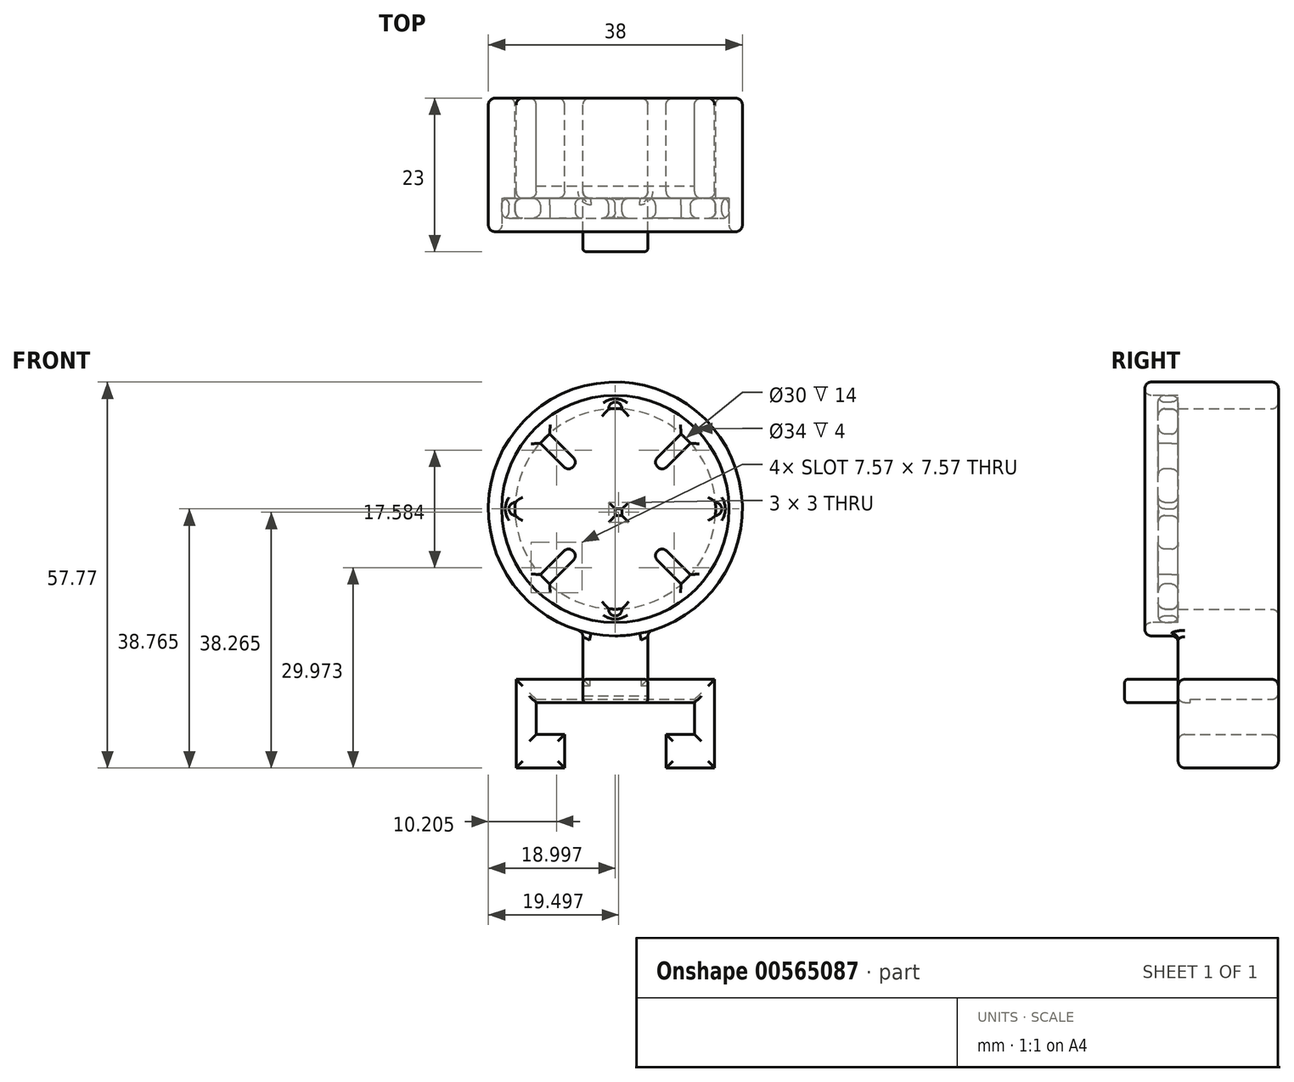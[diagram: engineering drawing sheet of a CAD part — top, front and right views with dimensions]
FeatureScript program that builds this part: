
annotation { "Feature Type Name" : "Feature", "Feature Type Description" : "" }
export const myFeature = defineFeature(function(context is Context, id is Id, definition is map)
    precondition{}
    {
        {
            var Q0;
            Q0=qCreatedBy(makeId("Front.planeOp"),FACE);
            var sketch = newSketch(context, id + "F0", { "sketchPlane" : qUnion([Q0])});
            skLineSegment(sketch, "E0", {"start": v(-3.95, 1.2) * mm, "end": v(-3.95, 6.2) * mm});
            skLineSegment(sketch, "E1", {"start": v(-3.95, 6.2) * mm, "end": v(-8.2, 6.2) * mm});
            skLineSegment(sketch, "E2", {"start": v(-8.2, 6.2) * mm, "end": v(-8.2, 11.46) * mm});
            skLineSegment(sketch, "E3", {"start": v(-8.2, 11.46) * mm, "end": v(15.5, 11.46) * mm});
            skLineSegment(sketch, "E4", {"start": v(15.5, 11.46) * mm, "end": v(15.5, 6.2) * mm});
            skLineSegment(sketch, "E5", {"start": v(15.5, 6.2) * mm, "end": v(11.25, 6.2) * mm});
            skLineSegment(sketch, "E6", {"start": v(11.25, 6.2) * mm, "end": v(11.25, 1.2) * mm});
            skLineSegment(sketch, "E7", {"start": v(18.5, 1.2) * mm, "end": v(18.5, 14.46) * mm});
            skLineSegment(sketch, "E8", {"start": v(18.5, 14.46) * mm, "end": v(-11.2, 14.46) * mm});
            skLineSegment(sketch, "E9", {"start": v(-11.2, 14.46) * mm, "end": v(-11.2, 1.2) * mm});
            skLineSegment(sketch, "E10", {"start": v(-11.2, 1.2) * mm, "end": v(-3.95, 1.2) * mm});
            skLineSegment(sketch, "E11", {"start": v(3.65, 14.46) * mm, "end": v(3.65, -1.28) * mm, "construction": true});
            skLineSegment(sketch, "E12", {"start": v(11.25, 1.2) * mm, "end": v(18.5, 1.2) * mm});
            skSolve(sketch);
        }
        {
            var Q0;
            Q0 = qSketchRegion(id + "F0", true);
            extrude(context, id + "F1", {"entities" : qUnion([Q0]), "depth" : 15 * mm, "offsetDistance" : 25 * mm});
        }
        {
            var Q0;
            Q0=makeQuery(id+"F1.opExtrude","SWEPT_FACE",FACE,{"disambiguationData":[OSD([sQuery(id+"F0.wireOp",EDGE,"E8")])]});
            var sketch = newSketch(context, id + "F2", { "sketchPlane" : qUnion([Q0])});
            skLineSegment(sketch, "E13.bottom", {"start": v(-1.2, -15) * mm, "end": v(8.5, -15) * mm});
            skLineSegment(sketch, "E13.top", {"start": v(-1.2, 0) * mm, "end": v(8.5, 0) * mm});
            skLineSegment(sketch, "E13.left", {"start": v(-1.2, -15) * mm, "end": v(-1.2, 0) * mm});
            skLineSegment(sketch, "E13.right", {"start": v(8.5, -15) * mm, "end": v(8.5, 0) * mm});
            skSolve(sketch);
        }
        {
            var Q0;
            Q0=makeQuery(id+"F2.imprint","IMPRINT",FACE,{"disambiguationData":[TD([[makeQuery(id+"F2.imprint","IMPRINT",EDGE,{"derivedFrom":sQuery(id+"F2.wireOp",EDGE,"E13.bottom")}),-1.0]])]});
            extrude(context, id + "F3", {"entities" : qUnion([Q0]), "operationType" : NewBodyOperationType.ADD, "depth" : 8 * mm, "offsetDistance" : 25 * mm});
        }
        {
            var Q0;
            Q0=makeQuery(id+"F3.boolean.opBoolean","MERGE",FACE,{"derivedFrom":[makeQuery(id+"F1.opExtrude","CAP_FACE",FACE,{"disambiguationData":[OSD([sQuery(id+"F0.wireOp",EDGE,"E0"),sQuery(id+"F0.wireOp",EDGE,"E1"),sQuery(id+"F0.wireOp",EDGE,"E2"),sQuery(id+"F0.wireOp",EDGE,"E3"),sQuery(id+"F0.wireOp",EDGE,"E4"),sQuery(id+"F0.wireOp",EDGE,"E5"),sQuery(id+"F0.wireOp",EDGE,"E6"),sQuery(id+"F0.wireOp",EDGE,"E7"),sQuery(id+"F0.wireOp",EDGE,"E8"),sQuery(id+"F0.wireOp",EDGE,"E9"),sQuery(id+"F0.wireOp",EDGE,"E10"),sQuery(id+"F0.wireOp",EDGE,"E12")])],"isStart":false}),makeQuery(id+"F3.opExtrude","SWEPT_FACE",FACE,{"disambiguationData":[OSD([sQuery(id+"F2.wireOp",EDGE,"E13.bottom")])]})]});
            var sketch = newSketch(context, id + "F4", { "sketchPlane" : qUnion([Q0])});
            skCircle(sketch, "E14", {"center": v(3.65, 39.97) * mm, "radius": 19 * mm});
            skPoint(sketch, "E14.centerSnap0", {"position": v(3.65, 22.46) * mm});
            skCircle(sketch, "E15", {"center": v(3.65, 39.97) * mm, "radius": 15 * mm});
            skSolve(sketch);
        }
        {
            var Q0;
            Q0 = qSketchRegion(id + "F4", true);
            extrude(context, id + "F5", {"entities" : qUnion([Q0]), "operationType" : NewBodyOperationType.ADD, "depth" : 5 * mm, "offsetDistance" : 25 * mm});
        }
        {
            var Q0;
            Q0=makeQuery(id+"F5.opExtrude","CAP_FACE",FACE,{"disambiguationData":[OSD([sQuery(id+"F4.wireOp",EDGE,"E14"),sQuery(id+"F4.wireOp",EDGE,"E15")])],"isStart":true});
            extrude(context, id + "F6", {"entities" : qUnion([Q0]), "operationType" : NewBodyOperationType.ADD, "depth" : 15 * mm, "offsetDistance" : 25 * mm});
        }
        {
            var Q0;
            Q0=makeQuery(id+"F5.opExtrude","CAP_FACE",FACE,{"disambiguationData":[OSD([sQuery(id+"F4.wireOp",EDGE,"E14"),sQuery(id+"F4.wireOp",EDGE,"E15")])],"isStart":false});
            var sketch = newSketch(context, id + "F7", { "sketchPlane" : qUnion([Q0])});
            skCircle(sketch, "E16", {"center": v(3.65, 39.97) * mm, "radius": 17 * mm});
            skSolve(sketch);
        }
        {
            var Q0;
            Q0 = qSketchRegion(id + "F7", true);
            extrude(context, id + "F8", {"entities" : qUnion([Q0]), "operationType" : NewBodyOperationType.REMOVE, "oppositeDirection" : true, "depth" : 5 * mm, "offsetDistance" : 25 * mm});
        }
        {
            var Q0;
            Q0=makeQuery(id+"F1.opExtrude","SWEPT_FACE",FACE,{"disambiguationData":[OSD([sQuery(id+"F0.wireOp",EDGE,"E3")])]});
            var sketch = newSketch(context, id + "F9", { "sketchPlane" : qUnion([Q0])});
            skLineSegment(sketch, "E17.bottom", {"start": v(-8.2, 15) * mm, "end": v(15.5, 15) * mm});
            skLineSegment(sketch, "E17.top", {"start": v(-8.2, 13.16) * mm, "end": v(15.5, 13.16) * mm});
            skLineSegment(sketch, "E17.left", {"start": v(-8.2, 15) * mm, "end": v(-8.2, 13.16) * mm});
            skLineSegment(sketch, "E17.right", {"start": v(15.5, 15) * mm, "end": v(15.5, 13.16) * mm});
            skSolve(sketch);
        }
        {
            var Q0;
            Q0 = qSketchRegion(id + "F9", true);
            extrude(context, id + "F10", {"entities" : qUnion([Q0]), "operationType" : NewBodyOperationType.ADD, "depth" : 0.5 * mm, "offsetDistance" : 25 * mm});
        }
        {
            var Q0;
            Q0=makeQuery(id+"F10.boolean.opBoolean","MERGE",FACE,{"derivedFrom":[makeQuery(id+"F3.boolean.opBoolean","MERGE",FACE,{"derivedFrom":[makeQuery(id+"F1.opExtrude","CAP_FACE",FACE,{"disambiguationData":[OSD([sQuery(id+"F0.wireOp",EDGE,"E0"),sQuery(id+"F0.wireOp",EDGE,"E1"),sQuery(id+"F0.wireOp",EDGE,"E2"),sQuery(id+"F0.wireOp",EDGE,"E3"),sQuery(id+"F0.wireOp",EDGE,"E4"),sQuery(id+"F0.wireOp",EDGE,"E5"),sQuery(id+"F0.wireOp",EDGE,"E6"),sQuery(id+"F0.wireOp",EDGE,"E7"),sQuery(id+"F0.wireOp",EDGE,"E8"),sQuery(id+"F0.wireOp",EDGE,"E9"),sQuery(id+"F0.wireOp",EDGE,"E10"),sQuery(id+"F0.wireOp",EDGE,"E12")])],"isStart":false}),makeQuery(id+"F3.opExtrude","SWEPT_FACE",FACE,{"disambiguationData":[OSD([sQuery(id+"F2.wireOp",EDGE,"E13.bottom")])]})]}),makeQuery(id+"F10.opExtrude","SWEPT_FACE",FACE,{"disambiguationData":[OSD([sQuery(id+"F9.wireOp",EDGE,"E17.bottom")])]})]});
            var sketch = newSketch(context, id + "F11", { "sketchPlane" : qUnion([Q0])});
            skLineSegment(sketch, "E18.bottom", {"start": v(-1.2, 14.46) * mm, "end": v(8.5, 14.46) * mm});
            skLineSegment(sketch, "E18.top", {"start": v(-1.2, 10.96) * mm, "end": v(8.5, 10.96) * mm});
            skLineSegment(sketch, "E18.left", {"start": v(-1.2, 14.46) * mm, "end": v(-1.2, 10.96) * mm});
            skLineSegment(sketch, "E18.right", {"start": v(8.5, 14.46) * mm, "end": v(8.5, 10.96) * mm});
            skSolve(sketch);
        }
        {
            var Q0;
            Q0=makeQuery(id+"F3.boolean.opBoolean","MERGE",FACE,{"derivedFrom":[makeQuery(id+"F1.opExtrude","CAP_FACE",FACE,{"disambiguationData":[OSD([sQuery(id+"F0.wireOp",EDGE,"E0"),sQuery(id+"F0.wireOp",EDGE,"E1"),sQuery(id+"F0.wireOp",EDGE,"E2"),sQuery(id+"F0.wireOp",EDGE,"E3"),sQuery(id+"F0.wireOp",EDGE,"E4"),sQuery(id+"F0.wireOp",EDGE,"E5"),sQuery(id+"F0.wireOp",EDGE,"E6"),sQuery(id+"F0.wireOp",EDGE,"E7"),sQuery(id+"F0.wireOp",EDGE,"E8"),sQuery(id+"F0.wireOp",EDGE,"E9"),sQuery(id+"F0.wireOp",EDGE,"E10"),sQuery(id+"F0.wireOp",EDGE,"E12")])],"isStart":false}),makeQuery(id+"F3.opExtrude","SWEPT_FACE",FACE,{"disambiguationData":[OSD([sQuery(id+"F2.wireOp",EDGE,"E13.bottom")])]})]});
            var Q1;
            Q1=makeQuery(id+"F5.opExtrude","CAP_FACE",FACE,{"disambiguationData":[OSD([sQuery(id+"F4.wireOp",EDGE,"E14"),sQuery(id+"F4.wireOp",EDGE,"E15")])],"isStart":false});
            var Q2;
            {var subQ0=sQuery(id+"F4.wireOp",EDGE,"E14");Q2=makeQuery(id+"F6.boolean.opBoolean","MERGE",FACE,{"derivedFrom":[makeQuery(id+"F5.opExtrude","SWEPT_FACE",FACE,{"disambiguationData":[OSD([subQ0])]}),makeQuery(id+"F6.opExtrude","SWEPT_FACE",FACE,{"disambiguationData":[OSD([subQ0])]})]});}
            var Q3;
            Q3=makeQuery(id+"F6.boolean.opBoolean","MERGE",FACE,{"derivedFrom":[makeQuery(id+"F3.boolean.opBoolean","MERGE",FACE,{"derivedFrom":[makeQuery(id+"F1.opExtrude","CAP_FACE",FACE,{"disambiguationData":[OSD([sQuery(id+"F0.wireOp",EDGE,"E0"),sQuery(id+"F0.wireOp",EDGE,"E1"),sQuery(id+"F0.wireOp",EDGE,"E2"),sQuery(id+"F0.wireOp",EDGE,"E3"),sQuery(id+"F0.wireOp",EDGE,"E4"),sQuery(id+"F0.wireOp",EDGE,"E5"),sQuery(id+"F0.wireOp",EDGE,"E6"),sQuery(id+"F0.wireOp",EDGE,"E7"),sQuery(id+"F0.wireOp",EDGE,"E8"),sQuery(id+"F0.wireOp",EDGE,"E9"),sQuery(id+"F0.wireOp",EDGE,"E10"),sQuery(id+"F0.wireOp",EDGE,"E12")])],"isStart":true}),makeQuery(id+"F3.opExtrude","SWEPT_FACE",FACE,{"disambiguationData":[OSD([sQuery(id+"F2.wireOp",EDGE,"E13.top")])]})]}),makeQuery(id+"F6.opExtrude","CAP_FACE",FACE,{"disambiguationData":[OSD([sQuery(id+"F4.wireOp",EDGE,"E14"),sQuery(id+"F4.wireOp",EDGE,"E15")])],"isStart":false})]});
            fillet(context, id + "F12", {"entities" : qUnion([Q0, Q1, Q2, Q3]), "radius" : 1 * mm, "tangentPropagation" : true, "allowEdgeOverflow" : false});
        }
        {
            var Q0;
            Q0 = qSketchRegion(id + "F11", true);
            extrude(context, id + "F13", {"entities" : qUnion([Q0]), "operationType" : NewBodyOperationType.ADD, "depth" : 8 * mm, "offsetDistance" : 25 * mm});
        }
        {
            var Q0;
            Q0=makeQuery(id+"F13.opExtrude","SWEPT_FACE",FACE,{"disambiguationData":[OSD([sQuery(id+"F11.wireOp",EDGE,"E18.top")])]});
            var Q1;
            Q1=makeQuery(id+"F13.opExtrude","CAP_FACE",FACE,{"disambiguationData":[OSD([sQuery(id+"F11.wireOp",EDGE,"E18.bottom"),sQuery(id+"F11.wireOp",EDGE,"E18.top"),sQuery(id+"F11.wireOp",EDGE,"E18.left"),sQuery(id+"F11.wireOp",EDGE,"E18.right")])],"isStart":false});
            var Q2;
            Q2=makeQuery(id+"F13.opExtrude","SWEPT_EDGE",EDGE,{"disambiguationData":[OSD([sQuery(id+"F0.wireOp",EDGE,"E8"),sQuery(id+"F2.wireOp",EDGE,"E13.bottom"),sQuery(id+"F2.wireOp",EDGE,"E13.right"),sQuery(id+"F11.wireOp",EDGE,"E18.bottom"),sQuery(id+"F11.wireOp",EDGE,"E18.right")])]});
            var Q3;
            Q3=makeQuery(id+"F13.opExtrude","SWEPT_EDGE",EDGE,{"disambiguationData":[OSD([sQuery(id+"F0.wireOp",EDGE,"E8"),sQuery(id+"F2.wireOp",EDGE,"E13.bottom"),sQuery(id+"F2.wireOp",EDGE,"E13.left"),sQuery(id+"F11.wireOp",EDGE,"E18.bottom"),sQuery(id+"F11.wireOp",EDGE,"E18.left")])]});
            fillet(context, id + "F14", {"entities" : qUnion([Q0, Q1, Q2, Q3]), "radius" : 0.5 * mm, "tangentPropagation" : true, "allowEdgeOverflow" : false});
        }
        {
            var Q0;
            Q0=makeQuery(id+"F8.boolean.opBoolean","COPY",FACE,{"derivedFrom":makeQuery(id+"F8.opExtrude","CAP_FACE",FACE,{"disambiguationData":[OSD([sQuery(id+"F7.wireOp",EDGE,"E16")])],"isStart":false})});
            var sketch = newSketch(context, id + "F15", { "sketchPlane" : qUnion([Q0])});
            skCircle(sketch, "E19", {"center": v(3.65, 39.97) * mm, "radius": 16.93 * mm});
            skCircle(sketch, "E20", {"center": v(3.65, 39.97) * mm, "radius": 14.91 * mm});
            skCircle(sketch, "E21", {"center": v(3.65, 39.97) * mm, "radius": 1.82 * mm});
            skLineSegment(sketch, "E22", {"start": v(3.65, 39.97) * mm, "end": v(3.65, 54.97) * mm});
            skArc(sketch, "E23.0.startCap", {"start": v(4.65, 39.97) * mm, "mid": v(3.65, 38.97) * mm, "end": v(2.65, 39.97) * mm});
            skArc(sketch, "E23.0.endCap", {"start": v(2.65, 54.97) * mm, "mid": v(3.65, 55.97) * mm, "end": v(4.65, 54.97) * mm});
            skLineSegment(sketch, "E23.0.left", {"start": v(2.65, 39.97) * mm, "end": v(2.65, 54.97) * mm});
            skLineSegment(sketch, "E23.0.right", {"start": v(4.65, 39.97) * mm, "end": v(4.65, 54.97) * mm});
            skLineSegment(sketch, "E24", {"start": v(3.65, 39.97) * mm, "end": v(18.56, 39.97) * mm});
            skLineSegment(sketch, "E25", {"start": v(3.65, 39.97) * mm, "end": v(-11.26, 39.97) * mm});
            skLineSegment(sketch, "E26", {"start": v(3.65, 39.97) * mm, "end": v(3.65, 24.97) * mm});
            skArc(sketch, "E27.0.startCap", {"start": v(3.65, 40.97) * mm, "mid": v(4.65, 39.97) * mm, "end": v(3.65, 38.97) * mm});
            skArc(sketch, "E27.0.endCap", {"start": v(-11.26, 38.97) * mm, "mid": v(-12.26, 39.97) * mm, "end": v(-11.26, 40.97) * mm});
            skLineSegment(sketch, "E27.0.left", {"start": v(3.65, 38.97) * mm, "end": v(-11.26, 38.97) * mm});
            skLineSegment(sketch, "E27.0.right", {"start": v(3.65, 40.97) * mm, "end": v(-11.26, 40.97) * mm});
            skArc(sketch, "E27.1.startCap", {"start": v(2.65, 39.97) * mm, "mid": v(3.65, 40.97) * mm, "end": v(4.65, 39.97) * mm});
            skArc(sketch, "E27.1.endCap", {"start": v(4.65, 24.97) * mm, "mid": v(3.65, 23.97) * mm, "end": v(2.65, 24.97) * mm});
            skLineSegment(sketch, "E27.1.left", {"start": v(4.65, 39.97) * mm, "end": v(4.65, 24.97) * mm});
            skLineSegment(sketch, "E27.1.right", {"start": v(2.65, 39.97) * mm, "end": v(2.65, 24.97) * mm});
            skArc(sketch, "E27.2.startCap", {"start": v(3.65, 38.97) * mm, "mid": v(2.65, 39.97) * mm, "end": v(3.65, 40.97) * mm});
            skArc(sketch, "E27.2.endCap", {"start": v(18.56, 40.97) * mm, "mid": v(19.56, 39.97) * mm, "end": v(18.56, 38.97) * mm});
            skLineSegment(sketch, "E27.2.left", {"start": v(3.65, 40.97) * mm, "end": v(18.56, 40.97) * mm});
            skLineSegment(sketch, "E27.2.right", {"start": v(3.65, 38.97) * mm, "end": v(18.56, 38.97) * mm});
            skSolve(sketch);
        }
        {
            var Q0;
            {var subQ0=sQuery(id+"F15.wireOp",EDGE,"E27.2.left");var subQ7=sQuery(id+"F15.wireOp",EDGE,"E20");var subQ10=makeQuery(id+"F15.imprint","INTERSECT",VERTEX,{"derivedFrom":[subQ7,subQ0]});Q0=makeQuery(id+"F15.imprint","IMPRINT",FACE,{"disambiguationData":[TD([[makeQuery(id+"F15.imprint","IMPRINT",EDGE,{"disambiguationData":[TD([[subQ10,-1.0]])],"derivedFrom":subQ7}),-1.0]])]});}
            var Q1;
            {var subQ3=sQuery(id+"F15.wireOp",EDGE,"E20");var subQ8=sQuery(id+"F15.wireOp",EDGE,"E23.0.left");var subQ9=makeQuery(id+"F15.imprint","INTERSECT",VERTEX,{"derivedFrom":[subQ3,subQ8]});Q1=makeQuery(id+"F15.imprint","IMPRINT",FACE,{"disambiguationData":[TD([[makeQuery(id+"F15.imprint","IMPRINT",EDGE,{"disambiguationData":[TD([[subQ9,-1.0]])],"derivedFrom":subQ3}),-1.0]])]});}
            var Q2;
            {var subQ1=sQuery(id+"F15.wireOp",EDGE,"E20");var subQ6=sQuery(id+"F15.wireOp",EDGE,"E27.0.left");var subQ9=makeQuery(id+"F15.imprint","INTERSECT",VERTEX,{"derivedFrom":[subQ1,subQ6]});Q2=makeQuery(id+"F15.imprint","IMPRINT",FACE,{"disambiguationData":[TD([[makeQuery(id+"F15.imprint","IMPRINT",EDGE,{"disambiguationData":[TD([[subQ9,-1.0]])],"derivedFrom":subQ1}),-1.0]])]});}
            var Q3;
            {var subQ6=sQuery(id+"F15.wireOp",EDGE,"E27.1.left");var subQ7=sQuery(id+"F15.wireOp",EDGE,"E20");var subQ8=makeQuery(id+"F15.imprint","INTERSECT",VERTEX,{"derivedFrom":[subQ7,subQ6]});Q3=makeQuery(id+"F15.imprint","IMPRINT",FACE,{"disambiguationData":[TD([[makeQuery(id+"F15.imprint","IMPRINT",EDGE,{"disambiguationData":[TD([[subQ8,-1.0]])],"derivedFrom":subQ7}),-1.0]])]});}
            var Q4;
            Q4=makeQuery(id+"F15.imprint","IMPRINT",FACE,{"disambiguationData":[TD([[makeQuery(id+"F15.imprint","IMPRINT",EDGE,{"derivedFrom":sQuery(id+"F15.wireOp",EDGE,"E19")}),1.0]])]});
            var Q5;
            {var subQ0=sQuery(id+"F15.wireOp",EDGE,"E24");var subQ1=sQuery(id+"F15.wireOp",EDGE,"E20");var subQ2=makeQuery(id+"F15.imprint","INTERSECT",VERTEX,{"derivedFrom":[subQ1,subQ0]});Q5=makeQuery(id+"F15.imprint","IMPRINT",FACE,{"disambiguationData":[TD([[makeQuery(id+"F15.imprint","IMPRINT",EDGE,{"disambiguationData":[TD([[subQ2,-1.0]])],"derivedFrom":subQ1}),1.0]])]});}
            var Q6;
            {var subQ0=sQuery(id+"F15.wireOp",EDGE,"E24");var subQ1=sQuery(id+"F15.wireOp",EDGE,"E20");var subQ2=makeQuery(id+"F15.imprint","INTERSECT",VERTEX,{"derivedFrom":[subQ1,subQ0]});Q6=makeQuery(id+"F15.imprint","IMPRINT",FACE,{"disambiguationData":[TD([[makeQuery(id+"F15.imprint","IMPRINT",EDGE,{"disambiguationData":[TD([[subQ2,1.0]])],"derivedFrom":subQ1}),1.0]])]});}
            var Q7;
            {var subQ0=sQuery(id+"F15.wireOp",EDGE,"E27.0.right");var subQ1=sQuery(id+"F15.wireOp",EDGE,"E21");var subQ2=makeQuery(id+"F15.imprint","INTERSECT",VERTEX,{"derivedFrom":[subQ1,subQ0]});Q7=makeQuery(id+"F15.imprint","IMPRINT",FACE,{"disambiguationData":[TD([[makeQuery(id+"F15.imprint","IMPRINT",EDGE,{"disambiguationData":[TD([[subQ2,-1.0]])],"derivedFrom":subQ1}),1.0]])]});}
            var Q8;
            Q8=makeQuery(id+"F15.imprint","IMPRINT",FACE,{"disambiguationData":[TD([[makeQuery(id+"F15.imprint","IMPRINT",EDGE,{"derivedFrom":sQuery(id+"F15.wireOp",EDGE,"E19")}),-1.0]])]});
            var Q9;
            {var subQ0=sQuery(id+"F15.wireOp",EDGE,"E26");var subQ1=sQuery(id+"F15.wireOp",EDGE,"E20");var subQ2=makeQuery(id+"F15.imprint","INTERSECT",VERTEX,{"derivedFrom":[subQ1,subQ0]});Q9=makeQuery(id+"F15.imprint","IMPRINT",FACE,{"disambiguationData":[TD([[makeQuery(id+"F15.imprint","IMPRINT",EDGE,{"disambiguationData":[TD([[subQ2,-1.0]])],"derivedFrom":subQ1}),1.0]])]});}
            var Q10;
            {var subQ0=sQuery(id+"F15.wireOp",EDGE,"E27.0.endCap");var subQ1=sQuery(id+"F4.wireOp",EDGE,"E15");var subQ2=makeQuery(id+"F8.boolean.opBoolean","INTERSECT",EDGE,{"derivedFrom":[makeQuery(id+"F6.boolean.opBoolean","MERGE",FACE,{"derivedFrom":[makeQuery(id+"F5.opExtrude","SWEPT_FACE",FACE,{"disambiguationData":[OSD([subQ1])]}),makeQuery(id+"F6.opExtrude","SWEPT_FACE",FACE,{"disambiguationData":[OSD([subQ1])]})]}),makeQuery(id+"F8.opExtrude","CAP_FACE",FACE,{"disambiguationData":[OSD([sQuery(id+"F7.wireOp",EDGE,"E16")])],"isStart":false})]});var subQ3=makeQuery(id+"F15.imprint","INTERSECT",VERTEX,{"disambiguationData":[OD(0.0)],"derivedFrom":[subQ2,subQ0]});Q10=makeQuery(id+"F15.imprint","IMPRINT",FACE,{"disambiguationData":[TD([[makeQuery(id+"F15.imprint","IMPRINT",EDGE,{"disambiguationData":[TD([[subQ3,-1.0]])],"derivedFrom":subQ0}),-1.0]])]});}
            var Q11;
            {var subQ0=sQuery(id+"F15.wireOp",EDGE,"E23.0.right");var subQ1=sQuery(id+"F15.wireOp",EDGE,"E21");var subQ2=makeQuery(id+"F15.imprint","INTERSECT",VERTEX,{"derivedFrom":[subQ1,subQ0]});Q11=makeQuery(id+"F15.imprint","IMPRINT",FACE,{"disambiguationData":[TD([[makeQuery(id+"F15.imprint","IMPRINT",EDGE,{"disambiguationData":[TD([[subQ2,-1.0]])],"derivedFrom":subQ1}),1.0]])]});}
            var Q12;
            {var subQ0=sQuery(id+"F15.wireOp",EDGE,"E23.0.right");var subQ1=sQuery(id+"F15.wireOp",EDGE,"E20");var subQ2=makeQuery(id+"F15.imprint","INTERSECT",VERTEX,{"derivedFrom":[subQ1,subQ0]});Q12=makeQuery(id+"F15.imprint","IMPRINT",FACE,{"disambiguationData":[TD([[makeQuery(id+"F15.imprint","IMPRINT",EDGE,{"disambiguationData":[TD([[subQ2,-1.0]])],"derivedFrom":subQ1}),1.0]])]});}
            var Q13;
            {var subQ0=sQuery(id+"F15.wireOp",EDGE,"E22");var subQ1=sQuery(id+"F15.wireOp",EDGE,"E20");var subQ2=makeQuery(id+"F15.imprint","INTERSECT",VERTEX,{"derivedFrom":[subQ1,subQ0]});Q13=makeQuery(id+"F15.imprint","IMPRINT",FACE,{"disambiguationData":[TD([[makeQuery(id+"F15.imprint","IMPRINT",EDGE,{"disambiguationData":[TD([[subQ2,-1.0]])],"derivedFrom":subQ1}),1.0]])]});}
            var Q14;
            {var subQ0=sQuery(id+"F15.wireOp",EDGE,"E27.1.right");var subQ1=sQuery(id+"F15.wireOp",EDGE,"E20");var subQ2=makeQuery(id+"F15.imprint","INTERSECT",VERTEX,{"derivedFrom":[subQ1,subQ0]});Q14=makeQuery(id+"F15.imprint","IMPRINT",FACE,{"disambiguationData":[TD([[makeQuery(id+"F15.imprint","IMPRINT",EDGE,{"disambiguationData":[TD([[subQ2,-1.0]])],"derivedFrom":subQ1}),1.0]])]});}
            var Q15;
            {var subQ0=sQuery(id+"F15.wireOp",EDGE,"E27.1.right");var subQ1=sQuery(id+"F15.wireOp",EDGE,"E21");var subQ2=makeQuery(id+"F15.imprint","INTERSECT",VERTEX,{"derivedFrom":[subQ1,subQ0]});Q15=makeQuery(id+"F15.imprint","IMPRINT",FACE,{"disambiguationData":[TD([[makeQuery(id+"F15.imprint","IMPRINT",EDGE,{"disambiguationData":[TD([[subQ2,-1.0]])],"derivedFrom":subQ1}),1.0]])]});}
            var Q16;
            {var subQ0=sQuery(id+"F15.wireOp",EDGE,"E25");var subQ1=sQuery(id+"F15.wireOp",EDGE,"E20");var subQ2=makeQuery(id+"F15.imprint","INTERSECT",VERTEX,{"derivedFrom":[subQ1,subQ0]});Q16=makeQuery(id+"F15.imprint","IMPRINT",FACE,{"disambiguationData":[TD([[makeQuery(id+"F15.imprint","IMPRINT",EDGE,{"disambiguationData":[TD([[subQ2,1.0]])],"derivedFrom":subQ1}),1.0]])]});}
            var Q17;
            {var subQ0=sQuery(id+"F15.wireOp",EDGE,"E27.2.endCap");var subQ1=sQuery(id+"F4.wireOp",EDGE,"E15");var subQ2=makeQuery(id+"F8.boolean.opBoolean","INTERSECT",EDGE,{"derivedFrom":[makeQuery(id+"F6.boolean.opBoolean","MERGE",FACE,{"derivedFrom":[makeQuery(id+"F5.opExtrude","SWEPT_FACE",FACE,{"disambiguationData":[OSD([subQ1])]}),makeQuery(id+"F6.opExtrude","SWEPT_FACE",FACE,{"disambiguationData":[OSD([subQ1])]})]}),makeQuery(id+"F8.opExtrude","CAP_FACE",FACE,{"disambiguationData":[OSD([sQuery(id+"F7.wireOp",EDGE,"E16")])],"isStart":false})]});var subQ3=makeQuery(id+"F15.imprint","INTERSECT",VERTEX,{"disambiguationData":[OD(0.0)],"derivedFrom":[subQ2,subQ0]});Q17=makeQuery(id+"F15.imprint","IMPRINT",FACE,{"disambiguationData":[TD([[makeQuery(id+"F15.imprint","IMPRINT",EDGE,{"disambiguationData":[TD([[subQ3,-1.0]])],"derivedFrom":subQ0}),-1.0]])]});}
            var Q18;
            {var subQ0=sQuery(id+"F15.wireOp",EDGE,"E25");var subQ1=sQuery(id+"F15.wireOp",EDGE,"E20");var subQ2=makeQuery(id+"F15.imprint","INTERSECT",VERTEX,{"derivedFrom":[subQ1,subQ0]});Q18=makeQuery(id+"F15.imprint","IMPRINT",FACE,{"disambiguationData":[TD([[makeQuery(id+"F15.imprint","IMPRINT",EDGE,{"disambiguationData":[TD([[subQ2,-1.0]])],"derivedFrom":subQ1}),1.0]])]});}
            var Q19;
            {var subQ1=sQuery(id+"F15.wireOp",EDGE,"E27.0.left");var subQ3=sQuery(id+"F15.wireOp",EDGE,"E27.1.right");var subQ4=makeQuery(id+"F15.imprint","INTERSECT",VERTEX,{"derivedFrom":[subQ1,subQ3]});Q19=makeQuery(id+"F15.imprint","IMPRINT",FACE,{"disambiguationData":[TD([[makeQuery(id+"F15.imprint","IMPRINT",EDGE,{"disambiguationData":[TD([[subQ4,1.0]])],"derivedFrom":subQ3}),1.0]])]});}
            var Q20;
            {var subQ0=sQuery(id+"F15.wireOp",EDGE,"E27.0.startCap");Q20=makeQuery(id+"F15.imprint","IMPRINT",FACE,{"disambiguationData":[TD([[makeQuery(id+"F15.imprint","IMPRINT",EDGE,{"derivedFrom":subQ0}),1.0]])]});}
            var Q21;
            {var subQ0=sQuery(id+"F15.wireOp",EDGE,"E25");var subQ1=sQuery(id+"F15.wireOp",EDGE,"E21");var subQ2=makeQuery(id+"F15.imprint","INTERSECT",VERTEX,{"derivedFrom":[subQ1,subQ0]});Q21=makeQuery(id+"F15.imprint","IMPRINT",FACE,{"disambiguationData":[TD([[makeQuery(id+"F15.imprint","IMPRINT",EDGE,{"disambiguationData":[TD([[subQ2,-1.0]])],"derivedFrom":subQ1}),1.0]])]});}
            var Q22;
            {var subQ0=sQuery(id+"F15.wireOp",EDGE,"E23.0.left");var subQ1=sQuery(id+"F15.wireOp",EDGE,"E21");var subQ2=makeQuery(id+"F15.imprint","INTERSECT",VERTEX,{"derivedFrom":[subQ1,subQ0]});Q22=makeQuery(id+"F15.imprint","IMPRINT",FACE,{"disambiguationData":[TD([[makeQuery(id+"F15.imprint","IMPRINT",EDGE,{"disambiguationData":[TD([[subQ2,-1.0]])],"derivedFrom":subQ1}),1.0]])]});}
            var Q23;
            {var subQ0=sQuery(id+"F15.wireOp",EDGE,"E27.2.left");var subQ1=sQuery(id+"F15.wireOp",EDGE,"E21");var subQ2=makeQuery(id+"F15.imprint","INTERSECT",VERTEX,{"derivedFrom":[subQ1,subQ0]});Q23=makeQuery(id+"F15.imprint","IMPRINT",FACE,{"disambiguationData":[TD([[makeQuery(id+"F15.imprint","IMPRINT",EDGE,{"disambiguationData":[TD([[subQ2,1.0]])],"derivedFrom":subQ1}),1.0]])]});}
            var Q24;
            {var subQ1=sQuery(id+"F15.wireOp",EDGE,"E23.0.left");var subQ3=sQuery(id+"F15.wireOp",EDGE,"E27.0.right");var subQ4=makeQuery(id+"F15.imprint","INTERSECT",VERTEX,{"derivedFrom":[subQ1,subQ3]});Q24=makeQuery(id+"F15.imprint","IMPRINT",FACE,{"disambiguationData":[TD([[makeQuery(id+"F15.imprint","IMPRINT",EDGE,{"disambiguationData":[TD([[subQ4,1.0]])],"derivedFrom":subQ1}),-1.0]])]});}
            var Q25;
            {var subQ6=sQuery(id+"F15.wireOp",EDGE,"E23.0.endCap");Q25=makeQuery(id+"F15.imprint","IMPRINT",FACE,{"disambiguationData":[TD([[makeQuery(id+"F15.imprint","IMPRINT",EDGE,{"derivedFrom":subQ6}),-1.0]])]});}
            var Q26;
            {var subQ3=sQuery(id+"F15.wireOp",EDGE,"E27.1.startCap");Q26=makeQuery(id+"F15.imprint","IMPRINT",FACE,{"disambiguationData":[TD([[makeQuery(id+"F15.imprint","IMPRINT",EDGE,{"derivedFrom":subQ3}),-1.0]])]});}
            var Q27;
            {var subQ0=sQuery(id+"F15.wireOp",EDGE,"E27.1.left");var subQ1=sQuery(id+"F15.wireOp",EDGE,"E21");var subQ2=makeQuery(id+"F15.imprint","INTERSECT",VERTEX,{"derivedFrom":[subQ1,subQ0]});Q27=makeQuery(id+"F15.imprint","IMPRINT",FACE,{"disambiguationData":[TD([[makeQuery(id+"F15.imprint","IMPRINT",EDGE,{"disambiguationData":[TD([[subQ2,-1.0]])],"derivedFrom":subQ1}),1.0]])]});}
            var Q28;
            {var subQ5=sQuery(id+"F15.wireOp",EDGE,"E27.1.endCap");Q28=makeQuery(id+"F15.imprint","IMPRINT",FACE,{"disambiguationData":[TD([[makeQuery(id+"F15.imprint","IMPRINT",EDGE,{"derivedFrom":subQ5}),-1.0]])]});}
            var Q29;
            {var subQ0=sQuery(id+"F15.wireOp",EDGE,"E24");var subQ1=sQuery(id+"F15.wireOp",EDGE,"E21");var subQ2=makeQuery(id+"F15.imprint","INTERSECT",VERTEX,{"derivedFrom":[subQ1,subQ0]});Q29=makeQuery(id+"F15.imprint","IMPRINT",FACE,{"disambiguationData":[TD([[makeQuery(id+"F15.imprint","IMPRINT",EDGE,{"disambiguationData":[TD([[subQ2,1.0]])],"derivedFrom":subQ1}),1.0]])]});}
            var Q30;
            {var subQ0=sQuery(id+"F15.wireOp",EDGE,"E27.0.left");var subQ1=sQuery(id+"F15.wireOp",EDGE,"E21");var subQ2=makeQuery(id+"F15.imprint","INTERSECT",VERTEX,{"derivedFrom":[subQ1,subQ0]});Q30=makeQuery(id+"F15.imprint","IMPRINT",FACE,{"disambiguationData":[TD([[makeQuery(id+"F15.imprint","IMPRINT",EDGE,{"disambiguationData":[TD([[subQ2,-1.0]])],"derivedFrom":subQ1}),1.0]])]});}
            var Q31;
            {var subQ0=sQuery(id+"F15.wireOp",EDGE,"E27.1.startCap");Q31=makeQuery(id+"F15.imprint","IMPRINT",FACE,{"disambiguationData":[TD([[makeQuery(id+"F15.imprint","IMPRINT",EDGE,{"derivedFrom":subQ0}),1.0]])]});}
            var Q32;
            {var subQ0=sQuery(id+"F15.wireOp",EDGE,"E26");var subQ1=sQuery(id+"F15.wireOp",EDGE,"E21");var subQ2=makeQuery(id+"F15.imprint","INTERSECT",VERTEX,{"derivedFrom":[subQ1,subQ0]});Q32=makeQuery(id+"F15.imprint","IMPRINT",FACE,{"disambiguationData":[TD([[makeQuery(id+"F15.imprint","IMPRINT",EDGE,{"disambiguationData":[TD([[subQ2,-1.0]])],"derivedFrom":subQ1}),1.0]])]});}
            var Q33;
            {var subQ0=sQuery(id+"F15.wireOp",EDGE,"E22");var subQ1=sQuery(id+"F15.wireOp",EDGE,"E21");var subQ2=makeQuery(id+"F15.imprint","INTERSECT",VERTEX,{"derivedFrom":[subQ1,subQ0]});Q33=makeQuery(id+"F15.imprint","IMPRINT",FACE,{"disambiguationData":[TD([[makeQuery(id+"F15.imprint","IMPRINT",EDGE,{"disambiguationData":[TD([[subQ2,-1.0]])],"derivedFrom":subQ1}),1.0]])]});}
            var Q34;
            {var subQ0=sQuery(id+"F15.wireOp",EDGE,"E27.2.left");var subQ1=sQuery(id+"F15.wireOp",EDGE,"E21");var subQ2=makeQuery(id+"F15.imprint","INTERSECT",VERTEX,{"derivedFrom":[subQ1,subQ0]});Q34=makeQuery(id+"F15.imprint","IMPRINT",FACE,{"disambiguationData":[TD([[makeQuery(id+"F15.imprint","IMPRINT",EDGE,{"disambiguationData":[TD([[subQ2,-1.0]])],"derivedFrom":subQ1}),1.0]])]});}
            var Q35;
            {var subQ0=sQuery(id+"F15.wireOp",EDGE,"E26");var subQ1=sQuery(id+"F15.wireOp",EDGE,"E20");var subQ2=makeQuery(id+"F15.imprint","INTERSECT",VERTEX,{"derivedFrom":[subQ1,subQ0]});Q35=makeQuery(id+"F15.imprint","IMPRINT",FACE,{"disambiguationData":[TD([[makeQuery(id+"F15.imprint","IMPRINT",EDGE,{"disambiguationData":[TD([[subQ2,-1.0]])],"derivedFrom":subQ1}),-1.0]])]});}
            var Q36;
            {var subQ6=sQuery(id+"F15.wireOp",EDGE,"E20");var subQ7=makeQuery(id+"F15.imprint","INTERSECT",VERTEX,{"derivedFrom":[subQ6,sQuery(id+"F15.wireOp",EDGE,"E24")]});Q36=makeQuery(id+"F15.imprint","IMPRINT",FACE,{"disambiguationData":[TD([[makeQuery(id+"F15.imprint","IMPRINT",EDGE,{"disambiguationData":[TD([[subQ7,-1.0]])],"derivedFrom":subQ6}),-1.0]])]});}
            var Q37;
            {var subQ0=sQuery(id+"F15.wireOp",EDGE,"E25");var subQ1=sQuery(id+"F15.wireOp",EDGE,"E22");var subQ2=makeQuery(id+"F15.imprint","INTERSECT",VERTEX,{"derivedFrom":[subQ1,sQuery(id+"F15.wireOp",EDGE,"E24"),subQ0,sQuery(id+"F15.wireOp",EDGE,"E26")]});Q37=makeQuery(id+"F15.imprint","IMPRINT",FACE,{"disambiguationData":[TD([[makeQuery(id+"F15.imprint","IMPRINT",EDGE,{"disambiguationData":[TD([[subQ2,-1.0]])],"derivedFrom":subQ0}),-1.0]])]});}
            var Q38;
            {var subQ0=sQuery(id+"F15.wireOp",EDGE,"E22");var subQ1=sQuery(id+"F15.wireOp",EDGE,"E20");var subQ2=makeQuery(id+"F15.imprint","INTERSECT",VERTEX,{"derivedFrom":[subQ1,subQ0]});Q38=makeQuery(id+"F15.imprint","IMPRINT",FACE,{"disambiguationData":[TD([[makeQuery(id+"F15.imprint","IMPRINT",EDGE,{"disambiguationData":[TD([[subQ2,-1.0]])],"derivedFrom":subQ1}),-1.0]])]});}
            var Q39;
            {var subQ0=sQuery(id+"F15.wireOp",EDGE,"E27.1.right");var subQ1=sQuery(id+"F15.wireOp",EDGE,"E20");var subQ2=makeQuery(id+"F15.imprint","INTERSECT",VERTEX,{"derivedFrom":[subQ1,subQ0]});Q39=makeQuery(id+"F15.imprint","IMPRINT",FACE,{"disambiguationData":[TD([[makeQuery(id+"F15.imprint","IMPRINT",EDGE,{"disambiguationData":[TD([[subQ2,-1.0]])],"derivedFrom":subQ1}),-1.0]])]});}
            var Q40;
            {var subQ0=sQuery(id+"F15.wireOp",EDGE,"E23.0.right");var subQ1=sQuery(id+"F15.wireOp",EDGE,"E20");var subQ2=makeQuery(id+"F15.imprint","INTERSECT",VERTEX,{"derivedFrom":[subQ1,subQ0]});Q40=makeQuery(id+"F15.imprint","IMPRINT",FACE,{"disambiguationData":[TD([[makeQuery(id+"F15.imprint","IMPRINT",EDGE,{"disambiguationData":[TD([[subQ2,-1.0]])],"derivedFrom":subQ1}),-1.0]])]});}
            var Q41;
            {var subQ6=sQuery(id+"F15.wireOp",EDGE,"E20");var subQ7=makeQuery(id+"F15.imprint","INTERSECT",VERTEX,{"derivedFrom":[subQ6,sQuery(id+"F15.wireOp",EDGE,"E25")]});Q41=makeQuery(id+"F15.imprint","IMPRINT",FACE,{"disambiguationData":[TD([[makeQuery(id+"F15.imprint","IMPRINT",EDGE,{"disambiguationData":[TD([[subQ7,1.0]])],"derivedFrom":subQ6}),-1.0]])]});}
            var Q42;
            {var subQ0=sQuery(id+"F15.wireOp",EDGE,"E26");var subQ1=sQuery(id+"F15.wireOp",EDGE,"E25");var subQ2=makeQuery(id+"F15.imprint","INTERSECT",VERTEX,{"derivedFrom":[sQuery(id+"F15.wireOp",EDGE,"E22"),sQuery(id+"F15.wireOp",EDGE,"E24"),subQ1,subQ0]});Q42=makeQuery(id+"F15.imprint","IMPRINT",FACE,{"disambiguationData":[TD([[makeQuery(id+"F15.imprint","IMPRINT",EDGE,{"disambiguationData":[TD([[subQ2,-1.0]])],"derivedFrom":subQ1}),1.0]])]});}
            var Q43;
            {var subQ3=sQuery(id+"F15.wireOp",EDGE,"E27.0.startCap");Q43=makeQuery(id+"F15.imprint","IMPRINT",FACE,{"disambiguationData":[TD([[makeQuery(id+"F15.imprint","IMPRINT",EDGE,{"derivedFrom":subQ3}),-1.0]])]});}
            extrude(context, id + "F16", {"entities" : qUnion([Q0, Q1, Q2, Q3, Q4, Q5, Q6, Q7, Q8, Q9, Q10, Q11, Q12, Q13, Q14, Q15, Q16, Q17, Q18, Q19, Q20, Q21, Q22, Q23, Q24, Q25, Q26, Q27, Q28, Q29, Q30, Q31, Q32, Q33, Q34, Q35, Q36, Q37, Q38, Q39, Q40, Q41, Q42, Q43]), "depth" : 3 * mm, "offsetDistance" : 25 * mm});
        }
        {
            var Q0;
            Q0=makeQuery(id+"F16.opExtrude","CAP_FACE",FACE,{"disambiguationData":[OSD([sQuery(id+"F7.wireOp",EDGE,"E16"),sQuery(id+"F15.wireOp",EDGE,"E20"),sQuery(id+"F15.wireOp",EDGE,"E21"),sQuery(id+"F15.wireOp",EDGE,"E23.0.left"),sQuery(id+"F15.wireOp",EDGE,"E23.0.right"),sQuery(id+"F15.wireOp",EDGE,"E27.0.left"),sQuery(id+"F15.wireOp",EDGE,"E27.0.right"),sQuery(id+"F15.wireOp",EDGE,"E27.1.left"),sQuery(id+"F15.wireOp",EDGE,"E27.1.right"),sQuery(id+"F15.wireOp",EDGE,"E27.2.left"),sQuery(id+"F15.wireOp",EDGE,"E27.2.right")])],"isStart":false});
            var sketch = newSketch(context, id + "F17", { "sketchPlane" : qUnion([Q0])});
            skLineSegment(sketch, "E28", {"start": v(14.2, 29.42) * mm, "end": v(-6.9, 29.42) * mm, "construction": true});
            skLineSegment(sketch, "E29", {"start": v(14.2, 50.5) * mm, "end": v(-6.9, 50.5) * mm, "construction": true});
            skLineSegment(sketch, "E30", {"start": v(-6.9, 50.5) * mm, "end": v(-3.36, 46.97) * mm});
            skLineSegment(sketch, "E31", {"start": v(14.2, 50.5) * mm, "end": v(10.66, 46.97) * mm});
            skLineSegment(sketch, "E32", {"start": v(-6.9, 29.42) * mm, "end": v(-3.36, 32.96) * mm});
            skLineSegment(sketch, "E33", {"start": v(14.2, 29.42) * mm, "end": v(10.66, 32.96) * mm});
            skArc(sketch, "E34.0.startCap", {"start": v(-7.6, 49.8) * mm, "mid": v(-7.6, 51.22) * mm, "end": v(-6.19, 51.22) * mm});
            skArc(sketch, "E34.0.endCap", {"start": v(-2.65, 47.68) * mm, "mid": v(-2.65, 46.27) * mm, "end": v(-4.07, 46.27) * mm});
            skLineSegment(sketch, "E34.0.left", {"start": v(-6.19, 51.22) * mm, "end": v(-2.65, 47.68) * mm});
            skLineSegment(sketch, "E34.0.right", {"start": v(-7.6, 49.8) * mm, "end": v(-4.07, 46.27) * mm});
            skArc(sketch, "E34.1.startCap", {"start": v(13.48, 51.22) * mm, "mid": v(14.9, 51.22) * mm, "end": v(14.9, 49.8) * mm});
            skArc(sketch, "E34.1.endCap", {"start": v(11.36, 46.27) * mm, "mid": v(9.95, 46.27) * mm, "end": v(9.95, 47.68) * mm});
            skLineSegment(sketch, "E34.1.left", {"start": v(14.9, 49.8) * mm, "end": v(11.36, 46.27) * mm});
            skLineSegment(sketch, "E34.1.right", {"start": v(13.48, 51.22) * mm, "end": v(9.95, 47.68) * mm});
            skArc(sketch, "E34.2.startCap", {"start": v(14.9, 30.13) * mm, "mid": v(14.9, 28.71) * mm, "end": v(13.48, 28.71) * mm});
            skArc(sketch, "E34.2.endCap", {"start": v(9.95, 32.25) * mm, "mid": v(9.95, 33.66) * mm, "end": v(11.36, 33.66) * mm});
            skLineSegment(sketch, "E34.2.left", {"start": v(13.48, 28.71) * mm, "end": v(9.95, 32.25) * mm});
            skLineSegment(sketch, "E34.2.right", {"start": v(14.9, 30.13) * mm, "end": v(11.36, 33.66) * mm});
            skArc(sketch, "E34.3.startCap", {"start": v(-6.19, 28.71) * mm, "mid": v(-7.6, 28.71) * mm, "end": v(-7.6, 30.13) * mm});
            skArc(sketch, "E34.3.endCap", {"start": v(-4.07, 33.66) * mm, "mid": v(-2.65, 33.66) * mm, "end": v(-2.65, 32.25) * mm});
            skLineSegment(sketch, "E34.3.left", {"start": v(-7.6, 30.13) * mm, "end": v(-4.07, 33.66) * mm});
            skLineSegment(sketch, "E34.3.right", {"start": v(-6.19, 28.71) * mm, "end": v(-2.65, 32.25) * mm});
            skSolve(sketch);
        }
        {
            var Q0;
            {var subQ5=sQuery(id+"F17.wireOp",EDGE,"E34.0.endCap");Q0=makeQuery(id+"F17.imprint","IMPRINT",FACE,{"disambiguationData":[TD([[makeQuery(id+"F17.imprint","IMPRINT",EDGE,{"derivedFrom":subQ5}),-1.0]])]});}
            var Q1;
            {var subQ6=sQuery(id+"F17.wireOp",EDGE,"E34.1.endCap");Q1=makeQuery(id+"F17.imprint","IMPRINT",FACE,{"disambiguationData":[TD([[makeQuery(id+"F17.imprint","IMPRINT",EDGE,{"derivedFrom":subQ6}),-1.0]])]});}
            var Q2;
            {var subQ6=sQuery(id+"F17.wireOp",EDGE,"E34.2.endCap");Q2=makeQuery(id+"F17.imprint","IMPRINT",FACE,{"disambiguationData":[TD([[makeQuery(id+"F17.imprint","IMPRINT",EDGE,{"derivedFrom":subQ6}),-1.0]])]});}
            var Q3;
            {var subQ1=sQuery(id+"F17.wireOp",EDGE,"E34.3.endCap");Q3=makeQuery(id+"F17.imprint","IMPRINT",FACE,{"disambiguationData":[TD([[makeQuery(id+"F17.imprint","IMPRINT",EDGE,{"derivedFrom":subQ1}),-1.0]])]});}
            extrude(context, id + "F18", {"entities" : qUnion([Q0, Q1, Q2, Q3]), "operationType" : NewBodyOperationType.ADD, "oppositeDirection" : true, "depth" : 3 * mm, "offsetDistance" : 25 * mm});
        }
        {
            var Q0;
            {var subQ0=sQuery(id+"F15.wireOp",EDGE,"E20");Q0=makeQuery(id+"F18.boolean.opBoolean","MERGE",FACE,{"derivedFrom":[makeQuery(id+"F16.opExtrude","CAP_FACE",FACE,{"disambiguationData":[OSD([sQuery(id+"F7.wireOp",EDGE,"E16"),subQ0,sQuery(id+"F15.wireOp",EDGE,"E21"),sQuery(id+"F15.wireOp",EDGE,"E23.0.left"),sQuery(id+"F15.wireOp",EDGE,"E23.0.right"),sQuery(id+"F15.wireOp",EDGE,"E27.0.left"),sQuery(id+"F15.wireOp",EDGE,"E27.0.right"),sQuery(id+"F15.wireOp",EDGE,"E27.1.left"),sQuery(id+"F15.wireOp",EDGE,"E27.1.right"),sQuery(id+"F15.wireOp",EDGE,"E27.2.left"),sQuery(id+"F15.wireOp",EDGE,"E27.2.right")])],"isStart":false}),makeQuery(id+"F18.opExtrude","CAP_FACE",FACE,{"disambiguationData":[OSD([subQ0,sQuery(id+"F17.wireOp",EDGE,"E34.0.endCap"),sQuery(id+"F17.wireOp",EDGE,"E34.0.left"),sQuery(id+"F17.wireOp",EDGE,"E34.0.right")])],"isStart":true}),makeQuery(id+"F18.opExtrude","CAP_FACE",FACE,{"disambiguationData":[OSD([subQ0,sQuery(id+"F17.wireOp",EDGE,"E34.1.endCap"),sQuery(id+"F17.wireOp",EDGE,"E34.1.left"),sQuery(id+"F17.wireOp",EDGE,"E34.1.right")])],"isStart":true}),makeQuery(id+"F18.opExtrude","CAP_FACE",FACE,{"disambiguationData":[OSD([subQ0,sQuery(id+"F17.wireOp",EDGE,"E34.2.endCap"),sQuery(id+"F17.wireOp",EDGE,"E34.2.left"),sQuery(id+"F17.wireOp",EDGE,"E34.2.right")])],"isStart":true}),makeQuery(id+"F18.opExtrude","CAP_FACE",FACE,{"disambiguationData":[OSD([subQ0,sQuery(id+"F17.wireOp",EDGE,"E34.3.endCap"),sQuery(id+"F17.wireOp",EDGE,"E34.3.left"),sQuery(id+"F17.wireOp",EDGE,"E34.3.right")])],"isStart":true})]});}
            var Q1;
            {var subQ0=sQuery(id+"F15.wireOp",EDGE,"E20");Q1=makeQuery(id+"F18.boolean.opBoolean","MERGE",FACE,{"derivedFrom":[makeQuery(id+"F16.opExtrude","CAP_FACE",FACE,{"disambiguationData":[OSD([sQuery(id+"F7.wireOp",EDGE,"E16"),subQ0,sQuery(id+"F15.wireOp",EDGE,"E21"),sQuery(id+"F15.wireOp",EDGE,"E23.0.left"),sQuery(id+"F15.wireOp",EDGE,"E23.0.right"),sQuery(id+"F15.wireOp",EDGE,"E27.0.left"),sQuery(id+"F15.wireOp",EDGE,"E27.0.right"),sQuery(id+"F15.wireOp",EDGE,"E27.1.left"),sQuery(id+"F15.wireOp",EDGE,"E27.1.right"),sQuery(id+"F15.wireOp",EDGE,"E27.2.left"),sQuery(id+"F15.wireOp",EDGE,"E27.2.right")])],"isStart":true}),makeQuery(id+"F18.opExtrude","CAP_FACE",FACE,{"disambiguationData":[OSD([subQ0,sQuery(id+"F17.wireOp",EDGE,"E34.0.endCap"),sQuery(id+"F17.wireOp",EDGE,"E34.0.left"),sQuery(id+"F17.wireOp",EDGE,"E34.0.right")])],"isStart":false}),makeQuery(id+"F18.opExtrude","CAP_FACE",FACE,{"disambiguationData":[OSD([subQ0,sQuery(id+"F17.wireOp",EDGE,"E34.1.endCap"),sQuery(id+"F17.wireOp",EDGE,"E34.1.left"),sQuery(id+"F17.wireOp",EDGE,"E34.1.right")])],"isStart":false}),makeQuery(id+"F18.opExtrude","CAP_FACE",FACE,{"disambiguationData":[OSD([subQ0,sQuery(id+"F17.wireOp",EDGE,"E34.2.endCap"),sQuery(id+"F17.wireOp",EDGE,"E34.2.left"),sQuery(id+"F17.wireOp",EDGE,"E34.2.right")])],"isStart":false}),makeQuery(id+"F18.opExtrude","CAP_FACE",FACE,{"disambiguationData":[OSD([subQ0,sQuery(id+"F17.wireOp",EDGE,"E34.3.endCap"),sQuery(id+"F17.wireOp",EDGE,"E34.3.left"),sQuery(id+"F17.wireOp",EDGE,"E34.3.right")])],"isStart":false})]});}
            fillet(context, id + "F19", {"entities" : qUnion([Q0, Q1]), "radius" : 1 * mm, "tangentPropagation" : true, "allowEdgeOverflow" : false});
        }
    });
